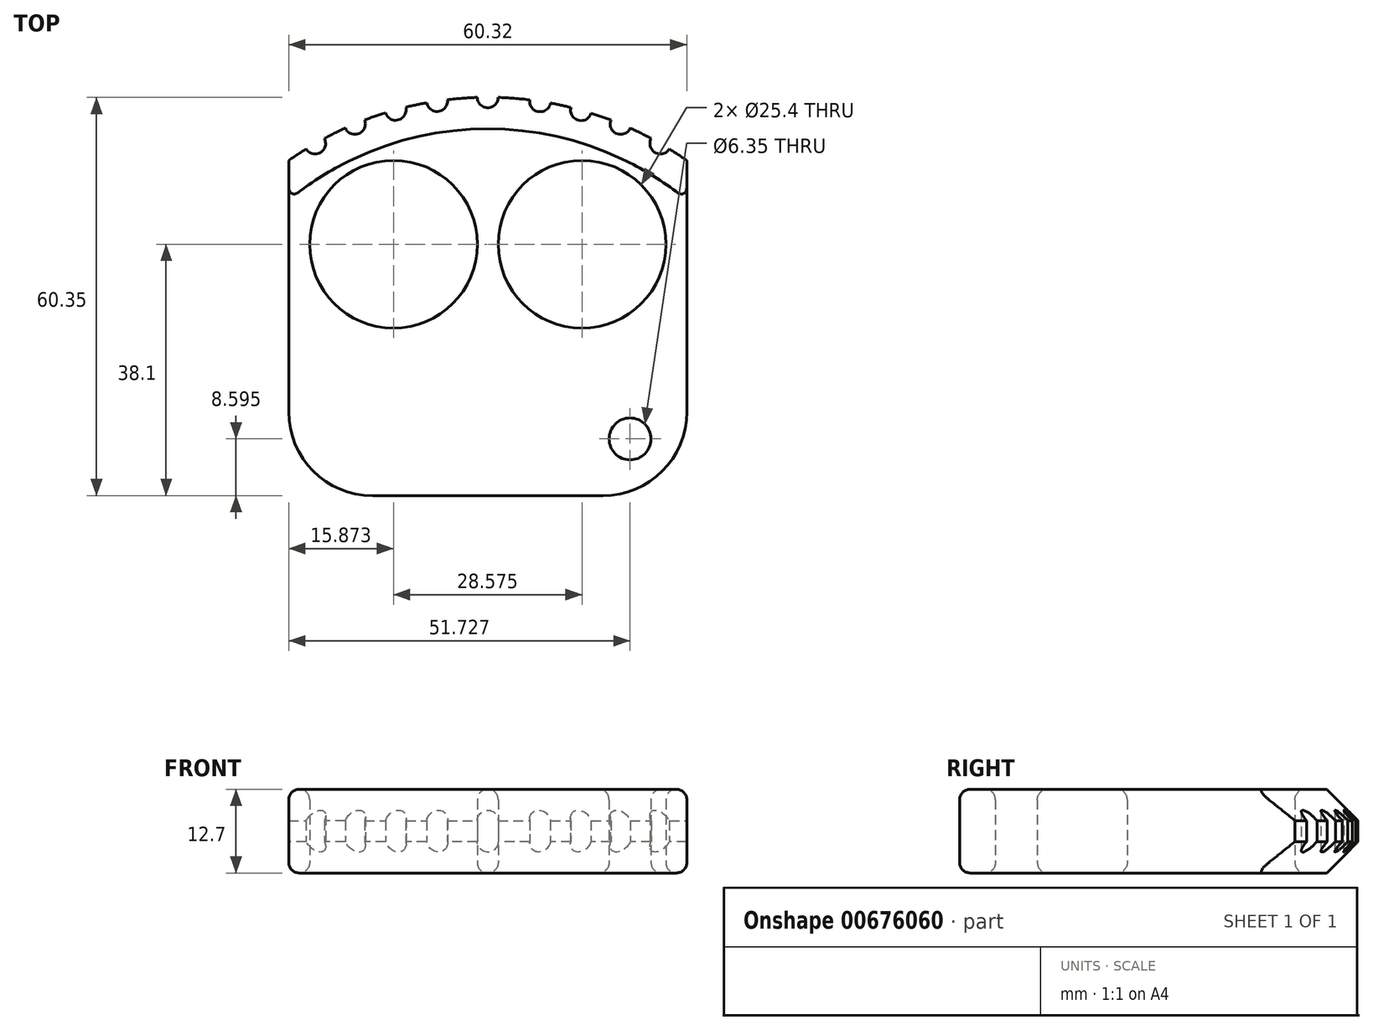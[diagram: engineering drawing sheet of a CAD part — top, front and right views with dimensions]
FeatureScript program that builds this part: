
annotation { "Feature Type Name" : "Feature", "Feature Type Description" : "" }
export const myFeature = defineFeature(function(context is Context, id is Id, definition is map)
    precondition{}
    {
        {
            var Q0;
            Q0=qCreatedBy(makeId("Top.planeOp"),FACE);
            var sketch = newSketch(context, id + "F0", { "sketchPlane" : qUnion([Q0])});
            skCircle(sketch, "E0", {"center": v(14.29, 0) * mm, "radius": 12.7 * mm});
            skCircle(sketch, "E1", {"center": v(-14.29, 0) * mm, "radius": 12.7 * mm});
            skArc(sketch, "E2", {"start": v(30.16, 12.7) * mm, "mid": v(0, 22.28) * mm, "end": v(-30.16, 12.7) * mm});
            skLineSegment(sketch, "E3", {"start": v(-30.16, 12.7) * mm, "end": v(-30.16, -25.4) * mm});
            skLineSegment(sketch, "E4", {"start": v(30.16, 12.7) * mm, "end": v(30.16, -25.4) * mm});
            skLineSegment(sketch, "E5", {"start": v(17.46, -38.1) * mm, "end": v(-17.46, -38.1) * mm});
            skPoint(sketch, "E6.visualSharp", {"position": v(30.16, -38.1) * mm});
            skArc(sketch, "E6.filletArc", {"start": v(17.46, -38.1) * mm, "mid": v(26.44, -34.38) * mm, "end": v(30.16, -25.4) * mm});
            skPoint(sketch, "E7.visualSharp", {"position": v(-30.16, -38.1) * mm});
            skArc(sketch, "E7.filletArc", {"start": v(-30.16, -25.4) * mm, "mid": v(-26.44, -34.38) * mm, "end": v(-17.46, -38.1) * mm});
            skArc(sketch, "E8", {"start": v(-27.51, 14.45) * mm, "mid": v(-25.36, 13.9) * mm, "end": v(-24.77, 16.04) * mm});
            skArc(sketch, "E9", {"start": v(-21.6, 17.61) * mm, "mid": v(-19.52, 16.78) * mm, "end": v(-18.66, 18.83) * mm});
            skArc(sketch, "E10", {"start": v(24.77, 16.04) * mm, "mid": v(25.36, 13.9) * mm, "end": v(27.51, 14.45) * mm});
            skArc(sketch, "E11", {"start": v(21.6, 17.61) * mm, "mid": v(19.52, 16.78) * mm, "end": v(18.66, 18.83) * mm});
            skArc(sketch, "E12", {"start": v(15.66, 19.88) * mm, "mid": v(13.71, 18.8) * mm, "end": v(12.6, 20.74) * mm});
            skArc(sketch, "E13", {"start": v(9.5, 21.4) * mm, "mid": v(7.7, 20.1) * mm, "end": v(6.36, 21.89) * mm});
            skArc(sketch, "E14", {"start": v(-15.49, 19.93) * mm, "mid": v(-13.54, 18.85) * mm, "end": v(-12.43, 20.78) * mm});
            skArc(sketch, "E15", {"start": v(-9.25, 21.45) * mm, "mid": v(-7.45, 20.14) * mm, "end": v(-6.11, 21.92) * mm});
            skArc(sketch, "E16", {"start": v(-1.59, 22.25) * mm, "mid": v(0, 20.7) * mm, "end": v(1.59, 22.25) * mm});
            skCircle(sketch, "E17", {"center": v(21.57, -29.5) * mm, "radius": 3.18 * mm});
            skSolve(sketch);
        }
        {
            var Q0;
            Q0=makeQuery(id+"F0.imprint","IMPRINT",FACE,{"disambiguationData":[TD([[makeQuery(id+"F0.imprint","IMPRINT",EDGE,{"derivedFrom":sQuery(id+"F0.wireOp",EDGE,"E0")}),-1.0]])]});
            extrude(context, id + "F1", {"entities" : qUnion([Q0]), "depth" : 12.7 * mm, "offsetDistance" : 25.4 * mm});
        }
        {
            var Q0;
            Q0=makeQuery(id+"F1.opExtrude","CAP_EDGE",EDGE,{"disambiguationData":[OSD([sQuery(id+"F0.wireOp",EDGE,"E5")])],"isStart":false});
            var Q1;
            Q1=makeQuery(id+"F1.opExtrude","CAP_EDGE",EDGE,{"disambiguationData":[OSD([sQuery(id+"F0.wireOp",EDGE,"E5")])],"isStart":true});
            var Q2;
            Q2=makeQuery(id+"F1.opExtrude","SWEPT_FACE",FACE,{"disambiguationData":[OSD([sQuery(id+"F0.wireOp",EDGE,"E1")])]});
            var Q3;
            Q3=makeQuery(id+"F1.opExtrude","SWEPT_FACE",FACE,{"disambiguationData":[OSD([sQuery(id+"F0.wireOp",EDGE,"E0")])]});
            fillet(context, id + "F2", {"entities" : qUnion([Q0, Q1, Q2, Q3]), "radius" : 1.59 * mm, "tangentPropagation" : true, "allowEdgeOverflow" : false});
        }
        {
            var Q0;
            {var subQ0=sQuery(id+"F0.wireOp",EDGE,"E2");Q0=makeQuery(id+"F1.opExtrude","CAP_EDGE",EDGE,{"disambiguationData":[OSD([subQ0]),TDD([makeQuery(id+"F0.imprint","IMPRINT",EDGE,{"disambiguationData":[TD([[makeQuery(id+"F0.imprint","INTERSECT",VERTEX,{"disambiguationData":[OD(1.0)],"derivedFrom":[subQ0,sQuery(id+"F0.wireOp",EDGE,"E8")]}),1.0]])],"derivedFrom":subQ0})])],"isStart":false});}
            var Q1;
            {var subQ0=sQuery(id+"F0.wireOp",EDGE,"E2");Q1=makeQuery(id+"F1.opExtrude","CAP_EDGE",EDGE,{"disambiguationData":[OSD([subQ0]),TDD([makeQuery(id+"F0.imprint","IMPRINT",EDGE,{"disambiguationData":[TD([[makeQuery(id+"F0.imprint","INTERSECT",VERTEX,{"disambiguationData":[OD(1.0)],"derivedFrom":[subQ0,sQuery(id+"F0.wireOp",EDGE,"E15")]}),1.0]])],"derivedFrom":subQ0})])],"isStart":true});}
            chamfer(context, id + "F3", {"entities" : qUnion([Q0, Q1]), "width" : 4.76 * mm, "tangentPropagation" : true});
        }
        {
            var Q0;
            Q0=makeQuery(id+"F0.imprint","IMPRINT",FACE,{"disambiguationData":[TD([[makeQuery(id+"F0.imprint","IMPRINT",EDGE,{"derivedFrom":sQuery(id+"F0.wireOp",EDGE,"E17")}),1.0]])]});
            extrude(context, id + "F4", {"entities" : qUnion([Q0]), "operationType" : NewBodyOperationType.REMOVE, "depth" : 25.4 * mm, "offsetDistance" : 25.4 * mm});
        }
        {
            var Q0;
            Q0=makeQuery(id+"F1.opExtrude","SWEPT_FACE",FACE,{"disambiguationData":[OSD([sQuery(id+"F0.wireOp",EDGE,"E17")])]});
            fillet(context, id + "F5", {"entities" : qUnion([Q0]), "radius" : 1.59 * mm, "tangentPropagation" : true, "allowEdgeOverflow" : false});
        }
    });
